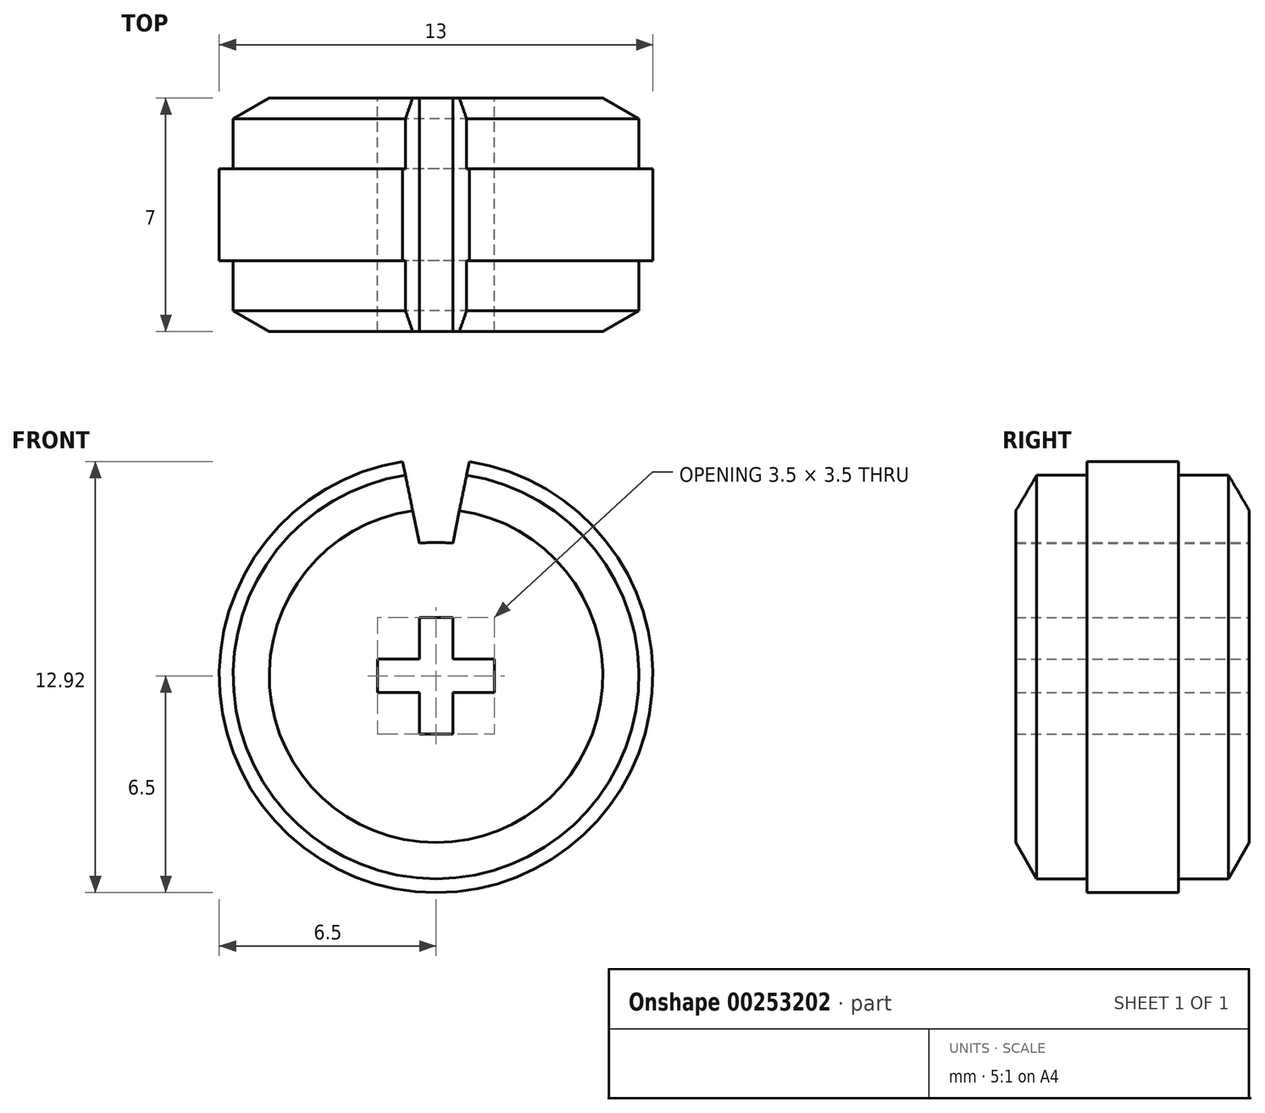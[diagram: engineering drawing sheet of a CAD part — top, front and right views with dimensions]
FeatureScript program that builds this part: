
annotation { "Feature Type Name" : "Feature", "Feature Type Description" : "" }
export const myFeature = defineFeature(function(context is Context, id is Id, definition is map)
    precondition{}
    {
        {
            var Q0;
            Q0=qCreatedBy(makeId("Front.planeOp"),FACE);
            var sketch = newSketch(context, id + "F0", { "sketchPlane" : qUnion([Q0])});
            skCircle(sketch, "E0", {"center": v(0, 0) * mm, "radius": 6.5 * mm});
            skLineSegment(sketch, "E1.0", {"start": v(-0.5, 0.5) * mm, "end": v(-0.5, 1.75) * mm});
            skLineSegment(sketch, "E1.1", {"start": v(-0.5, 1.75) * mm, "end": v(0.5, 1.75) * mm});
            skLineSegment(sketch, "E1.2", {"start": v(0.5, 1.75) * mm, "end": v(0.5, 0.5) * mm});
            skLineSegment(sketch, "E1.3", {"start": v(0.5, 0.5) * mm, "end": v(1.75, 0.5) * mm});
            skLineSegment(sketch, "E1.4", {"start": v(1.75, 0.5) * mm, "end": v(1.75, -0.5) * mm});
            skLineSegment(sketch, "E1.5", {"start": v(1.75, -0.5) * mm, "end": v(0.5, -0.5) * mm});
            skLineSegment(sketch, "E1.6", {"start": v(0.5, -0.5) * mm, "end": v(0.5, -1.75) * mm});
            skLineSegment(sketch, "E1.7", {"start": v(0.5, -1.75) * mm, "end": v(-0.5, -1.75) * mm});
            skLineSegment(sketch, "E1.8", {"start": v(-0.5, -1.75) * mm, "end": v(-0.5, -0.5) * mm});
            skLineSegment(sketch, "E1.9", {"start": v(-0.5, -0.5) * mm, "end": v(-1.75, -0.5) * mm});
            skLineSegment(sketch, "E1.10", {"start": v(-1.75, -0.5) * mm, "end": v(-1.75, 0.5) * mm});
            skLineSegment(sketch, "E1.11", {"start": v(-1.75, 0.5) * mm, "end": v(-0.5, 0.5) * mm});
            skLineSegment(sketch, "E2", {"start": v(-0.5, 0.5) * mm, "end": v(0.5, -0.5) * mm, "construction": true});
            skLineSegment(sketch, "E3", {"start": v(-0.5, -0.5) * mm, "end": v(0.5, 0.5) * mm, "construction": true});
            skSolve(sketch);
        }
        {
            var Q0;
            Q0 = qSketchRegion(id + "F0", true);
            extrude(context, id + "F1", {"entities" : qUnion([Q0]), "depth" : 7 * mm});
        }
        {
            var Q0;
            Q0=qCreatedBy(makeId("Right.planeOp"),FACE);
            var sketch = newSketch(context, id + "F2", { "sketchPlane" : qUnion([Q0])});
            skLineSegment(sketch, "E4", {"start": v(0, 0) * mm, "end": v(5.2, 0) * mm, "construction": true});
            skLineSegment(sketch, "E5", {"start": v(-7, 5) * mm, "end": v(-6.38, 6.08) * mm});
            skLineSegment(sketch, "E6", {"start": v(-6.38, 6.08) * mm, "end": v(-4.88, 6.08) * mm});
            skLineSegment(sketch, "E7", {"start": v(-4.88, 6.08) * mm, "end": v(-4.88, 6.5) * mm});
            skLineSegment(sketch, "E8", {"start": v(-4.88, 6.5) * mm, "end": v(-2.12, 6.5) * mm});
            skLineSegment(sketch, "E9", {"start": v(-2.12, 6.5) * mm, "end": v(-2.12, 6.08) * mm});
            skLineSegment(sketch, "E10", {"start": v(-2.12, 6.08) * mm, "end": v(-0.63, 6.08) * mm});
            skLineSegment(sketch, "E11", {"start": v(-0.62, 6.08) * mm, "end": v(0, 5) * mm});
            skLineSegment(sketch, "E12", {"start": v(0, 5) * mm, "end": v(0, 8) * mm});
            skLineSegment(sketch, "E13", {"start": v(0, 8) * mm, "end": v(-7, 8) * mm});
            skLineSegment(sketch, "E14", {"start": v(-7, 8) * mm, "end": v(-7, 5) * mm});
            skPoint(sketch, "E15", {"position": v(0, 6.5) * mm});
            skPoint(sketch, "E16.positionSnap0", {"position": v(-7, 6.5) * mm});
            skSolve(sketch);
        }
        {
            var Q0;
            Q0 = qSketchRegion(id + "F2", true);
            var Q1;
            Q1=sQuery(id+"F2.wireOp",EDGE,"E4");
            revolve(context, id + "F3", {"operationType" : NewBodyOperationType.REMOVE, "entities" : qUnion([Q0]), "axis" : qUnion([Q1]), "revolveType" : RevolveType.FULL, "oppositeDirection" : true});
        }
        {
            var Q0;
            Q0=qCreatedBy(makeId("Front.planeOp"),FACE);
            var sketch = newSketch(context, id + "F4", { "sketchPlane" : qUnion([Q0])});
            skLineSegment(sketch, "E17", {"start": v(1, 6.42) * mm, "end": v(0.5, 3.97) * mm});
            skArc(sketch, "E18", {"start": v(0.5, 3.97) * mm, "mid": v(0, 4) * mm, "end": v(-0.5, 3.97) * mm});
            skLineSegment(sketch, "E19", {"start": v(-0.5, 3.97) * mm, "end": v(-1, 6.42) * mm});
            skArc(sketch, "E20", {"start": v(1, 6.42) * mm, "mid": v(0, 6.5) * mm, "end": v(-1, 6.42) * mm});
            skPoint(sketch, "E21", {"position": v(0, 6.5) * mm});
            skPoint(sketch, "E21.positionSnap0", {"position": v(0, 6.5) * mm});
            skPoint(sketch, "E22", {"position": v(0, 4) * mm});
            skSolve(sketch);
        }
        {
            var Q0;
            Q0 = qSketchRegion(id + "F4", true);
            extrude(context, id + "F5", {"entities" : qUnion([Q0]), "operationType" : NewBodyOperationType.REMOVE, "endBound" : BoundingType.THROUGH_ALL, "depth" : 25 * mm});
        }
    });
